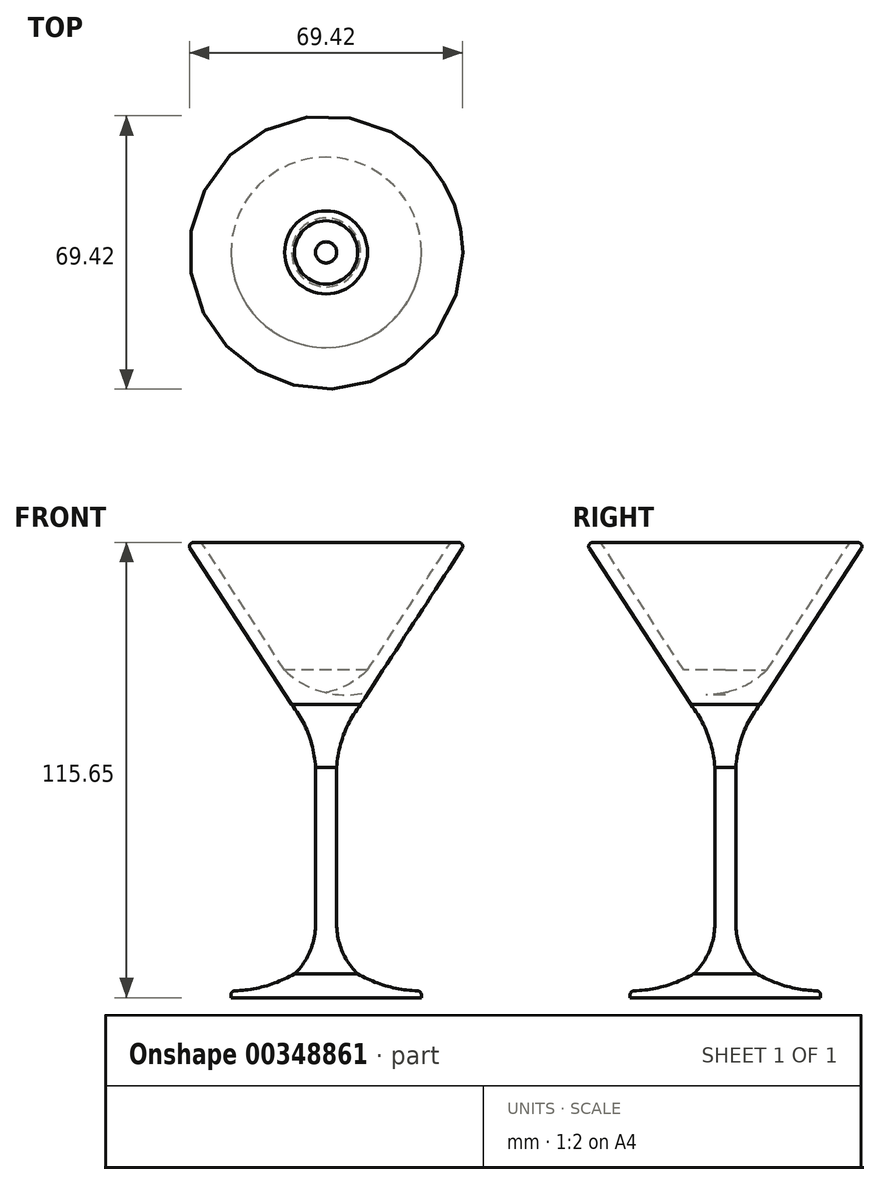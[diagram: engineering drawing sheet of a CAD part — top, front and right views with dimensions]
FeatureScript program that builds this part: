
annotation { "Feature Type Name" : "Feature", "Feature Type Description" : "" }
export const myFeature = defineFeature(function(context is Context, id is Id, definition is map)
    precondition{}
    {
        {
            var Q0;
            Q0=qCreatedBy(makeId("Front.planeOp"),FACE);
            var sketch = newSketch(context, id + "F0", { "sketchPlane" : qUnion([Q0])});
            skLineSegment(sketch, "E0", {"start": v(35.56, 66.9) * mm, "end": v(8.76, 25.74) * mm});
            skArc(sketch, "E1", {"start": v(8.76, 25.74) * mm, "mid": v(4.49, 18.2) * mm, "end": v(2.68, 9.71) * mm});
            skLineSegment(sketch, "E2", {"start": v(2.68, 9.71) * mm, "end": v(2.68, -30.03) * mm});
            skArc(sketch, "E3", {"start": v(2.68, -30.03) * mm, "mid": v(4.08, -36.92) * mm, "end": v(8.04, -42.72) * mm});
            skArc(sketch, "E4", {"start": v(8.04, -42.72) * mm, "mid": v(15.84, -45.92) * mm, "end": v(24.2, -47.05) * mm});
            skLineSegment(sketch, "E5", {"start": v(24.2, -47.05) * mm, "end": v(24.2, -48.75) * mm});
            skLineSegment(sketch, "E6", {"start": v(24.2, -48.75) * mm, "end": v(0, -48.75) * mm});
            skLineSegment(sketch, "E7", {"start": v(0, -48.75) * mm, "end": v(0, 28.73) * mm});
            skArc(sketch, "E8", {"start": v(0, 28.73) * mm, "mid": v(5.67, 30.88) * mm, "end": v(10.54, 34.47) * mm});
            skLineSegment(sketch, "E9", {"start": v(10.54, 34.47) * mm, "end": v(31.65, 66.9) * mm});
            skLineSegment(sketch, "E10", {"start": v(31.65, 66.9) * mm, "end": v(35.56, 66.9) * mm});
            skLineSegment(sketch, "E11", {"start": v(0, 98.7) * mm, "end": v(0, -199.78) * mm, "construction": true});
            skSolve(sketch);
        }
        {
            var Q0;
            Q0 = qSketchRegion(id + "F0", true);
            var Q1;
            Q1 = qConstructionFilter(qBodyType(qCreatedBy(id + "F0" ,EDGE), BodyType.WIRE), ConstructionObject.NO);
            var Q2;
            Q2=sQuery(id+"F0.wireOp",EDGE,"E11");
            revolve(context, id + "F1", {"entities" : qUnion([Q0]), "surfaceEntities" : qUnion([Q1]), "axis" : qUnion([Q2]), "revolveType" : RevolveType.FULL});
        }
        {
            var Q0;
            Q0=makeQuery(id+"F1.opRevolve","SWEPT_FACE",FACE,{"disambiguationData":[OSD([sQuery(id+"F0.wireOp",EDGE,"E10")])]});
            var Q1;
            Q1=makeQuery(id+"F1.opRevolve","SWEPT_EDGE",EDGE,{"disambiguationData":[OSD([sQuery(id+"F0.wireOp",EDGE,"E0"),sQuery(id+"F0.wireOp",EDGE,"E10")])]});
            var Q2;
            Q2=makeQuery(id+"F1.opRevolve","SWEPT_EDGE",EDGE,{"disambiguationData":[OSD([sQuery(id+"F0.wireOp",EDGE,"E4"),sQuery(id+"F0.wireOp",EDGE,"E5")])]});
            fillet(context, id + "F2", {"entities" : qUnion([Q0, Q1, Q2]), "radius" : 1 * mm, "tangentPropagation" : true, "allowEdgeOverflow" : false});
        }
    });
